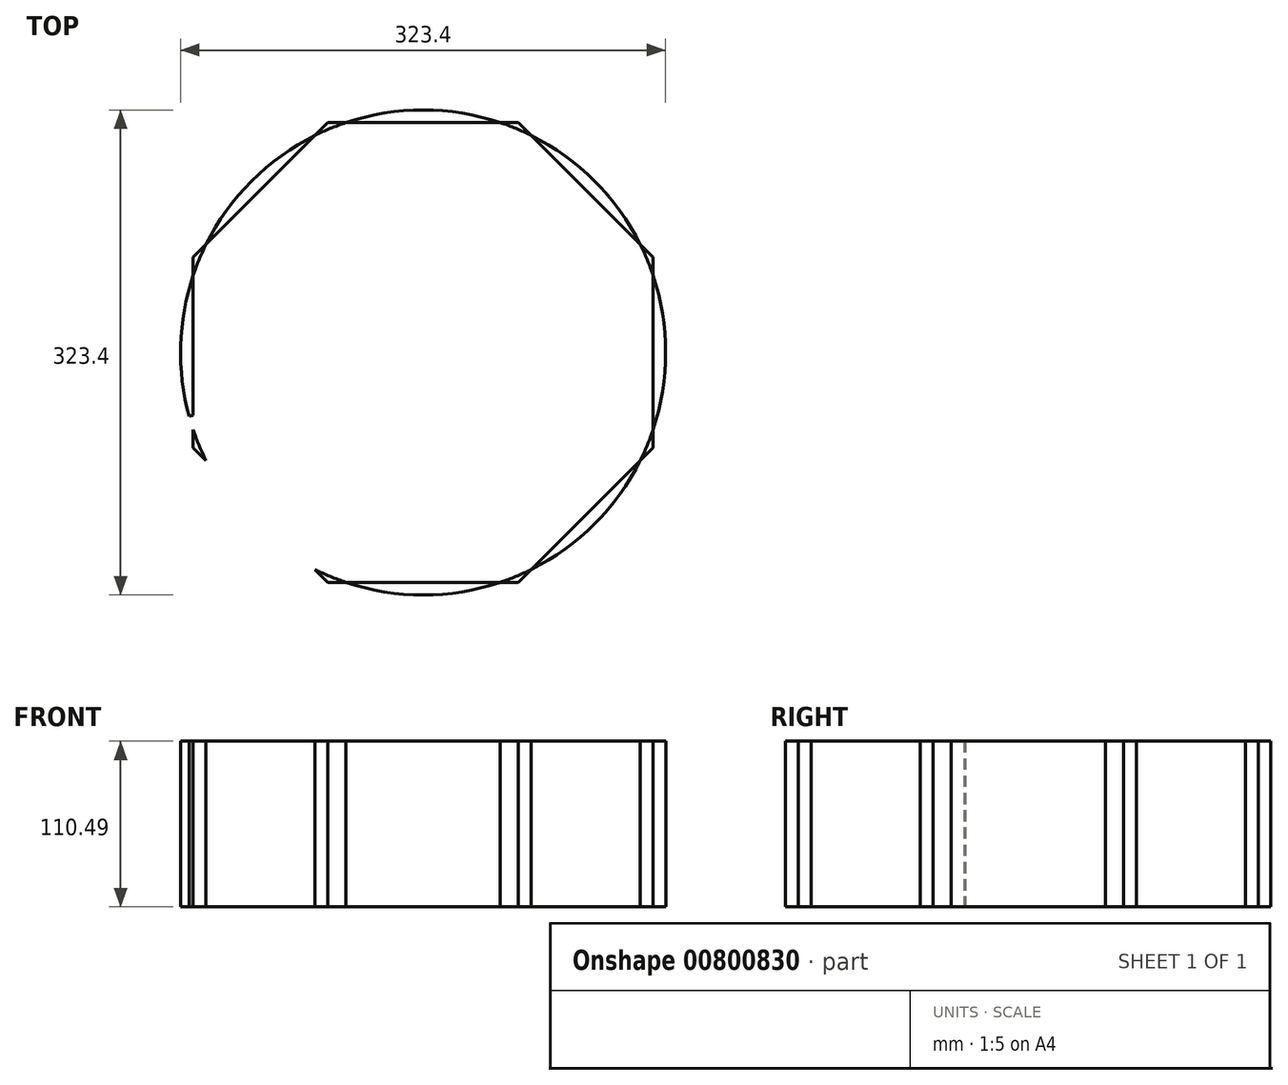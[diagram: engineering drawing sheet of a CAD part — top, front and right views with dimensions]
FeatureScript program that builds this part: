
annotation { "Feature Type Name" : "Feature", "Feature Type Description" : "" }
export const myFeature = defineFeature(function(context is Context, id is Id, definition is map)
    precondition{}
    {
        {
            var Q0;
            Q0=qCreatedBy(makeId("Top.planeOp"),FACE);
            var sketch = newSketch(context, id + "F0", { "sketchPlane" : qUnion([Q0])});
            skCircle(sketch, "E0.cCircle", {"center": v(0, 0) * mm, "radius": 153.3 * mm, "construction": true});
            skLineSegment(sketch, "E0.0", {"start": v(-153.3, -63.5) * mm, "end": v(-153.3, 63.5) * mm});
            skLineSegment(sketch, "E0.1", {"start": v(-153.3, 63.5) * mm, "end": v(-63.5, 153.3) * mm});
            skLineSegment(sketch, "E0.2", {"start": v(-63.5, 153.3) * mm, "end": v(63.5, 153.3) * mm});
            skLineSegment(sketch, "E0.3", {"start": v(63.5, 153.3) * mm, "end": v(153.3, 63.5) * mm});
            skLineSegment(sketch, "E0.4", {"start": v(153.3, 63.5) * mm, "end": v(153.3, -63.5) * mm});
            skLineSegment(sketch, "E0.5", {"start": v(153.3, -63.5) * mm, "end": v(63.5, -153.3) * mm});
            skLineSegment(sketch, "E0.6", {"start": v(63.5, -153.3) * mm, "end": v(-63.5, -153.3) * mm});
            skLineSegment(sketch, "E0.7", {"start": v(-63.5, -153.3) * mm, "end": v(-153.3, -63.5) * mm});
            skPoint(sketch, "E0.0.midPoint", {"position": v(-153.3, 0) * mm});
            skCircle(sketch, "E1", {"center": v(0, 0) * mm, "radius": 161.7 * mm});
            skArc(sketch, "E2", {"start": v(0, -161.7) * mm, "mid": v(-98.1, -128.54) * mm, "end": v(-155.97, -42.67) * mm});
            skLineSegment(sketch, "E3", {"start": v(-153.3, -63.5) * mm, "end": v(-153.3, -43.18) * mm});
            skLineSegment(sketch, "E4", {"start": v(0, 0) * mm, "end": v(-155.97, -42.67) * mm});
            skLineSegment(sketch, "E5", {"start": v(0, 0) * mm, "end": v(-153.3, -43.18) * mm});
            skSolve(sketch);
        }
        {
            var Q0;
            {var subQ0=sQuery(id+"F0.wireOp",EDGE,"E0.1");var subQ1=sQuery(id+"F0.wireOp",EDGE,"E0.0");var subQ2=makeQuery(id+"F0.imprint","INTERSECT",VERTEX,{"derivedFrom":[subQ1,subQ0]});Q0=makeQuery(id+"F0.imprint","IMPRINT",FACE,{"disambiguationData":[TD([[makeQuery(id+"F0.imprint","IMPRINT",EDGE,{"disambiguationData":[TD([[subQ2,1.0]])],"derivedFrom":subQ1}),-1.0]])]});}
            var Q1;
            {var subQ0=sQuery(id+"F0.wireOp",EDGE,"E1");var subQ1=sQuery(id+"F0.wireOp",EDGE,"E0.1");var subQ2=makeQuery(id+"F0.imprint","INTERSECT",VERTEX,{"disambiguationData":[OD(0.0)],"derivedFrom":[subQ1,subQ0]});Q1=makeQuery(id+"F0.imprint","IMPRINT",FACE,{"disambiguationData":[TD([[makeQuery(id+"F0.imprint","IMPRINT",EDGE,{"disambiguationData":[TD([[subQ2,-1.0]])],"derivedFrom":subQ1}),1.0]])]});}
            var Q2;
            {var subQ0=sQuery(id+"F0.wireOp",EDGE,"E0.2");var subQ1=sQuery(id+"F0.wireOp",EDGE,"E0.1");var subQ2=makeQuery(id+"F0.imprint","INTERSECT",VERTEX,{"derivedFrom":[subQ1,subQ0]});Q2=makeQuery(id+"F0.imprint","IMPRINT",FACE,{"disambiguationData":[TD([[makeQuery(id+"F0.imprint","IMPRINT",EDGE,{"disambiguationData":[TD([[subQ2,1.0]])],"derivedFrom":subQ1}),-1.0]])]});}
            var Q3;
            {var subQ0=sQuery(id+"F0.wireOp",EDGE,"E1");var subQ1=sQuery(id+"F0.wireOp",EDGE,"E0.2");var subQ2=makeQuery(id+"F0.imprint","INTERSECT",VERTEX,{"disambiguationData":[OD(0.0)],"derivedFrom":[subQ1,subQ0]});Q3=makeQuery(id+"F0.imprint","IMPRINT",FACE,{"disambiguationData":[TD([[makeQuery(id+"F0.imprint","IMPRINT",EDGE,{"disambiguationData":[TD([[subQ2,-1.0]])],"derivedFrom":subQ1}),1.0]])]});}
            var Q4;
            {var subQ0=sQuery(id+"F0.wireOp",EDGE,"E0.3");var subQ1=sQuery(id+"F0.wireOp",EDGE,"E0.2");var subQ2=makeQuery(id+"F0.imprint","INTERSECT",VERTEX,{"derivedFrom":[subQ1,subQ0]});Q4=makeQuery(id+"F0.imprint","IMPRINT",FACE,{"disambiguationData":[TD([[makeQuery(id+"F0.imprint","IMPRINT",EDGE,{"disambiguationData":[TD([[subQ2,1.0]])],"derivedFrom":subQ1}),-1.0]])]});}
            var Q5;
            {var subQ0=sQuery(id+"F0.wireOp",EDGE,"E1");var subQ1=sQuery(id+"F0.wireOp",EDGE,"E0.3");var subQ2=makeQuery(id+"F0.imprint","INTERSECT",VERTEX,{"disambiguationData":[OD(0.0)],"derivedFrom":[subQ1,subQ0]});Q5=makeQuery(id+"F0.imprint","IMPRINT",FACE,{"disambiguationData":[TD([[makeQuery(id+"F0.imprint","IMPRINT",EDGE,{"disambiguationData":[TD([[subQ2,-1.0]])],"derivedFrom":subQ1}),1.0]])]});}
            var Q6;
            {var subQ0=sQuery(id+"F0.wireOp",EDGE,"E0.4");var subQ1=sQuery(id+"F0.wireOp",EDGE,"E0.3");var subQ2=makeQuery(id+"F0.imprint","INTERSECT",VERTEX,{"derivedFrom":[subQ1,subQ0]});Q6=makeQuery(id+"F0.imprint","IMPRINT",FACE,{"disambiguationData":[TD([[makeQuery(id+"F0.imprint","IMPRINT",EDGE,{"disambiguationData":[TD([[subQ2,1.0]])],"derivedFrom":subQ1}),-1.0]])]});}
            var Q7;
            {var subQ0=sQuery(id+"F0.wireOp",EDGE,"E1");var subQ1=sQuery(id+"F0.wireOp",EDGE,"E0.4");var subQ2=makeQuery(id+"F0.imprint","INTERSECT",VERTEX,{"disambiguationData":[OD(0.0)],"derivedFrom":[subQ1,subQ0]});Q7=makeQuery(id+"F0.imprint","IMPRINT",FACE,{"disambiguationData":[TD([[makeQuery(id+"F0.imprint","IMPRINT",EDGE,{"disambiguationData":[TD([[subQ2,-1.0]])],"derivedFrom":subQ1}),1.0]])]});}
            var Q8;
            {var subQ0=sQuery(id+"F0.wireOp",EDGE,"E0.5");var subQ1=sQuery(id+"F0.wireOp",EDGE,"E0.4");var subQ2=makeQuery(id+"F0.imprint","INTERSECT",VERTEX,{"derivedFrom":[subQ1,subQ0]});Q8=makeQuery(id+"F0.imprint","IMPRINT",FACE,{"disambiguationData":[TD([[makeQuery(id+"F0.imprint","IMPRINT",EDGE,{"disambiguationData":[TD([[subQ2,1.0]])],"derivedFrom":subQ1}),-1.0]])]});}
            var Q9;
            {var subQ0=sQuery(id+"F0.wireOp",EDGE,"E1");var subQ1=sQuery(id+"F0.wireOp",EDGE,"E0.5");var subQ2=makeQuery(id+"F0.imprint","INTERSECT",VERTEX,{"disambiguationData":[OD(0.0)],"derivedFrom":[subQ1,subQ0]});Q9=makeQuery(id+"F0.imprint","IMPRINT",FACE,{"disambiguationData":[TD([[makeQuery(id+"F0.imprint","IMPRINT",EDGE,{"disambiguationData":[TD([[subQ2,-1.0]])],"derivedFrom":subQ1}),1.0]])]});}
            var Q10;
            {var subQ0=sQuery(id+"F0.wireOp",EDGE,"E0.6");var subQ1=sQuery(id+"F0.wireOp",EDGE,"E0.5");var subQ2=makeQuery(id+"F0.imprint","INTERSECT",VERTEX,{"derivedFrom":[subQ1,subQ0]});Q10=makeQuery(id+"F0.imprint","IMPRINT",FACE,{"disambiguationData":[TD([[makeQuery(id+"F0.imprint","IMPRINT",EDGE,{"disambiguationData":[TD([[subQ2,1.0]])],"derivedFrom":subQ1}),-1.0]])]});}
            var Q11;
            {var subQ0=sQuery(id+"F0.wireOp",EDGE,"E1");var subQ1=sQuery(id+"F0.wireOp",EDGE,"E0.6");var subQ2=makeQuery(id+"F0.imprint","INTERSECT",VERTEX,{"disambiguationData":[OD(0.0)],"derivedFrom":[subQ1,subQ0]});Q11=makeQuery(id+"F0.imprint","IMPRINT",FACE,{"disambiguationData":[TD([[makeQuery(id+"F0.imprint","IMPRINT",EDGE,{"disambiguationData":[TD([[subQ2,-1.0]])],"derivedFrom":subQ1}),1.0]])]});}
            var Q12;
            {var subQ0=sQuery(id+"F0.wireOp",EDGE,"E0.7");var subQ1=sQuery(id+"F0.wireOp",EDGE,"E0.6");var subQ2=makeQuery(id+"F0.imprint","INTERSECT",VERTEX,{"derivedFrom":[subQ1,subQ0]});Q12=makeQuery(id+"F0.imprint","IMPRINT",FACE,{"disambiguationData":[TD([[makeQuery(id+"F0.imprint","IMPRINT",EDGE,{"disambiguationData":[TD([[subQ2,1.0]])],"derivedFrom":subQ1}),-1.0]])]});}
            var Q13;
            {var subQ0=sQuery(id+"F0.wireOp",EDGE,"E1");var subQ1=sQuery(id+"F0.wireOp",EDGE,"E0.7");var subQ2=makeQuery(id+"F0.imprint","INTERSECT",VERTEX,{"disambiguationData":[OD(0.0)],"derivedFrom":[subQ1,subQ0]});Q13=makeQuery(id+"F0.imprint","IMPRINT",FACE,{"disambiguationData":[TD([[makeQuery(id+"F0.imprint","IMPRINT",EDGE,{"disambiguationData":[TD([[subQ2,-1.0]])],"derivedFrom":subQ1}),1.0]])]});}
            var Q14;
            {var subQ0=sQuery(id+"F0.wireOp",EDGE,"E3");var subQ1=sQuery(id+"F0.wireOp",EDGE,"E0.7");var subQ2=makeQuery(id+"F0.imprint","INTERSECT",VERTEX,{"derivedFrom":[subQ1,subQ0]});Q14=makeQuery(id+"F0.imprint","IMPRINT",FACE,{"disambiguationData":[TD([[makeQuery(id+"F0.imprint","IMPRINT",EDGE,{"disambiguationData":[TD([[subQ2,1.0]])],"derivedFrom":subQ1}),-1.0]])]});}
            var Q15;
            {var subQ0=sQuery(id+"F0.wireOp",EDGE,"E1");var subQ1=sQuery(id+"F0.wireOp",EDGE,"E0.0");var subQ2=makeQuery(id+"F0.imprint","INTERSECT",VERTEX,{"derivedFrom":[subQ1,subQ0]});Q15=makeQuery(id+"F0.imprint","IMPRINT",FACE,{"disambiguationData":[TD([[makeQuery(id+"F0.imprint","IMPRINT",EDGE,{"disambiguationData":[TD([[subQ2,1.0]])],"derivedFrom":subQ1}),1.0]])]});}
            var Q16;
            {var subQ3=sQuery(id+"F0.wireOp",EDGE,"E4");var subQ5=sQuery(id+"F0.wireOp",EDGE,"E1");var subQ6=makeQuery(id+"F0.imprint","INTERSECT",VERTEX,{"derivedFrom":[subQ5,subQ3]});Q16=makeQuery(id+"F0.imprint","IMPRINT",FACE,{"disambiguationData":[TD([[makeQuery(id+"F0.imprint","IMPRINT",EDGE,{"disambiguationData":[TD([[subQ6,-1.0]])],"derivedFrom":subQ5}),1.0]])]});}
            extrude(context, id + "F1", {"entities" : qUnion([Q0, Q1, Q2, Q3, Q4, Q5, Q6, Q7, Q8, Q9, Q10, Q11, Q12, Q13, Q14, Q15, Q16]), "depth" : 110.49 * mm, "offsetDistance" : 25.4 * mm});
        }
    });
